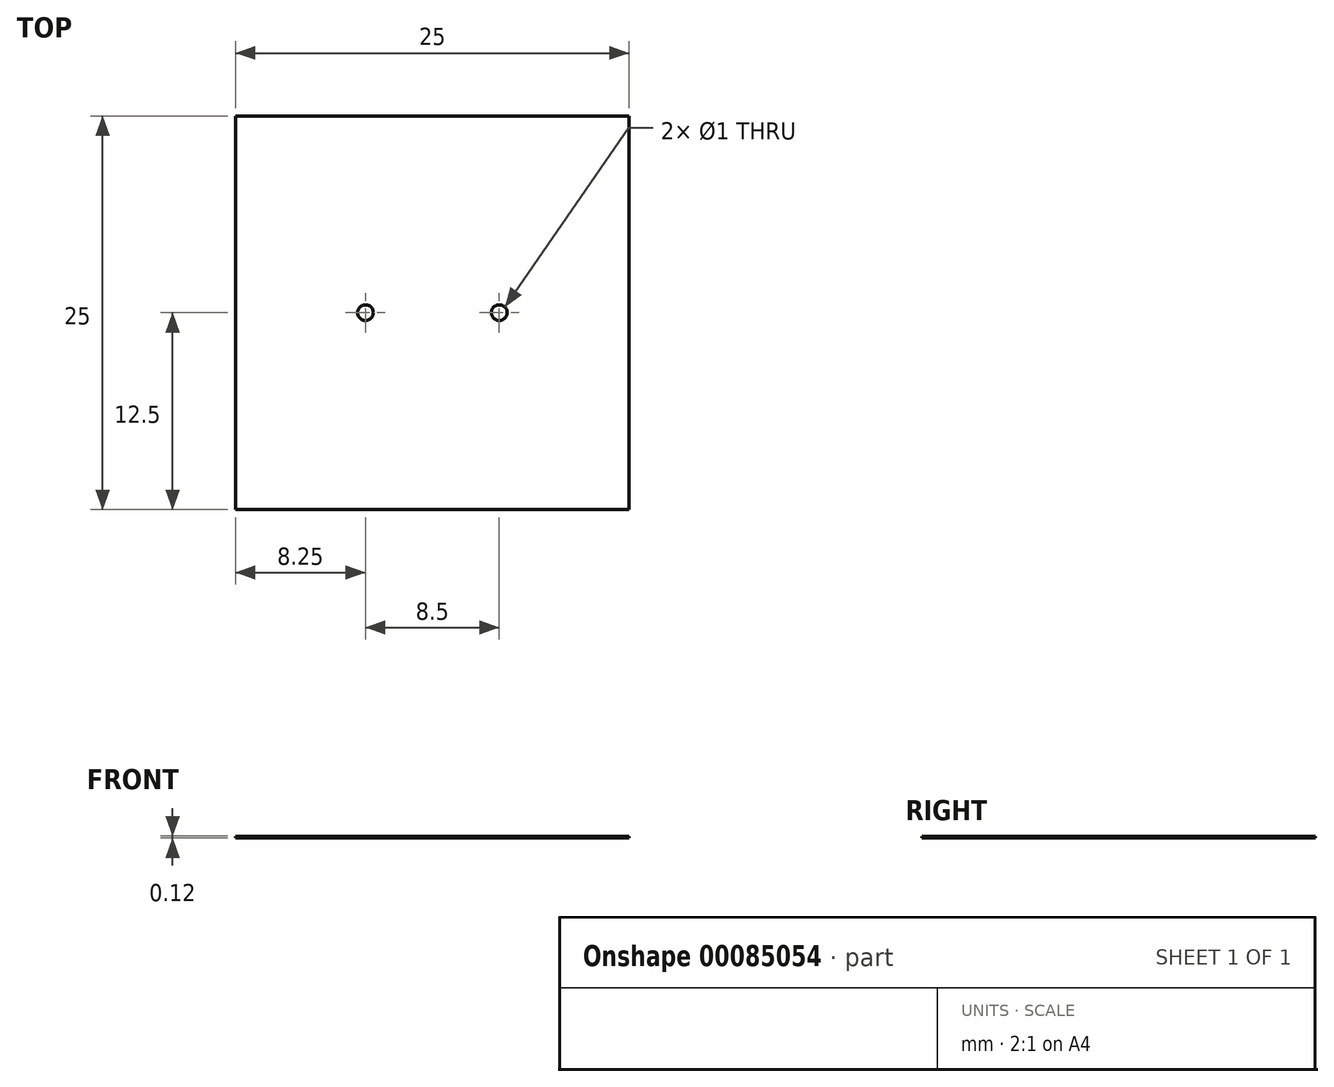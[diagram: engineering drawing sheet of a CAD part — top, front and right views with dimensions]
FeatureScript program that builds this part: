
annotation { "Feature Type Name" : "Feature", "Feature Type Description" : "" }
export const myFeature = defineFeature(function(context is Context, id is Id, definition is map)
    precondition{}
    {
        {
            var Q0;
            Q0=qCreatedBy(makeId("Top.planeOp"),FACE);
            var sketch = newSketch(context, id + "F0", { "sketchPlane" : qUnion([Q0])});
            skLineSegment(sketch, "E0.bottom", {"start": v(12.5, -12.5) * mm, "end": v(-12.5, -12.5) * mm});
            skLineSegment(sketch, "E0.top", {"start": v(12.5, 12.5) * mm, "end": v(-12.5, 12.5) * mm});
            skLineSegment(sketch, "E0.left", {"start": v(12.5, -12.5) * mm, "end": v(12.5, 12.5) * mm});
            skLineSegment(sketch, "E0.right", {"start": v(-12.5, -12.5) * mm, "end": v(-12.5, 12.5) * mm});
            skPoint(sketch, "E0.middle", {"position": v(0, 0) * mm});
            skCircle(sketch, "E1", {"center": v(-4.25, 0) * mm, "radius": 0.5 * mm});
            skLineSegment(sketch, "E2", {"start": v(0, 0) * mm, "end": v(0, 19.9) * mm, "construction": true});
            skCircle(sketch, "E3.MirrorC", {"center": v(4.25, 0) * mm, "radius": 0.5 * mm});
            skSolve(sketch);
        }
        {
            var Q0;
            Q0 = qSketchRegion(id + "F0", true);
            extrude(context, id + "F1", {"entities" : qUnion([Q0]), "depth" : .117 * mm});
        }
    });
